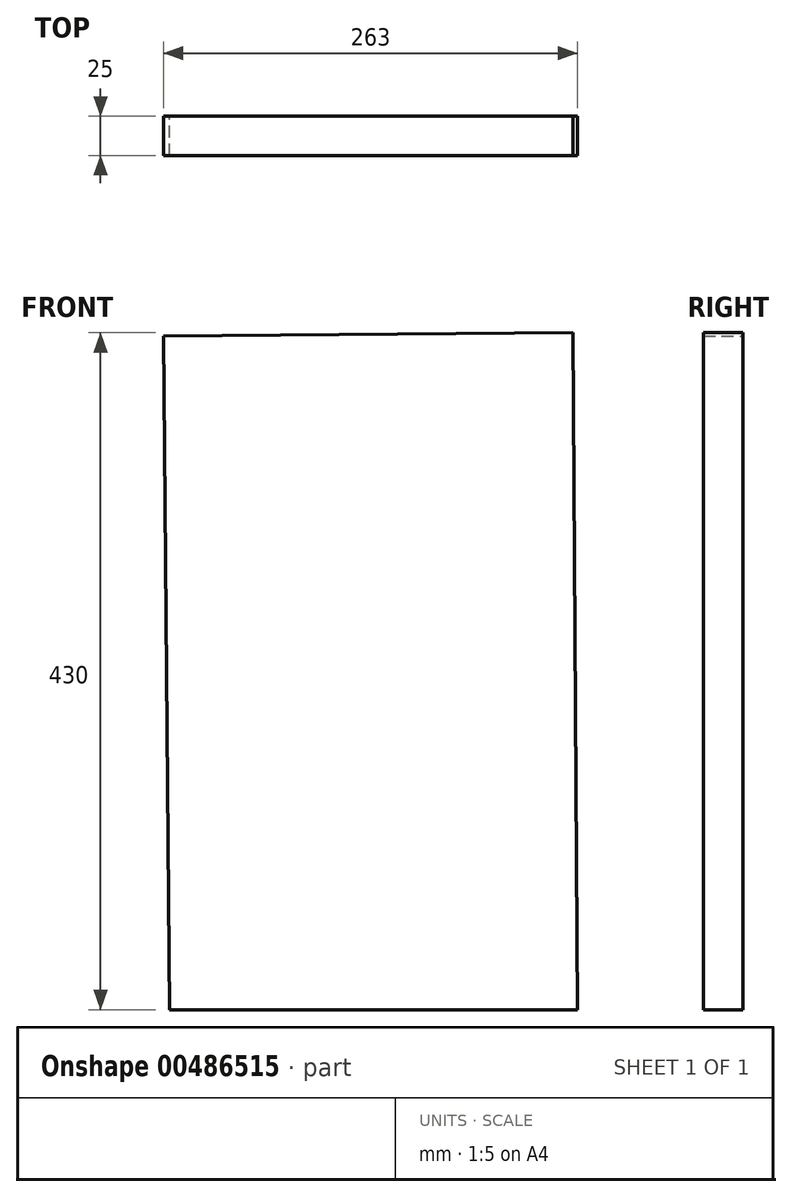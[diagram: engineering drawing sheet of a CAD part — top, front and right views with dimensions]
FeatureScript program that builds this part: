
annotation { "Feature Type Name" : "Feature", "Feature Type Description" : "" }
export const myFeature = defineFeature(function(context is Context, id is Id, definition is map)
    precondition{}
    {
        {
            var Q0;
            Q0=qCreatedBy(makeId("Front.planeOp"),FACE);
            var sketch = newSketch(context, id + "F0", { "sketchPlane" : qUnion([Q0])});
            skArc(sketch, "E0", {"start": v(777, 1224.97) * mm, "mid": v(1501.6, 922.35) * mm, "end": v(1800, 196) * mm});
            skLineSegment(sketch, "E1", {"start": v(1800, 196) * mm, "end": v(1800, 0) * mm});
            skLineSegment(sketch, "E2", {"start": v(1800, 0) * mm, "end": v(0, 0) * mm});
            skLineSegment(sketch, "E3", {"start": v(0, 0) * mm, "end": v(0, 611.22) * mm});
            skCircle(sketch, "E4", {"center": v(195, 100) * mm, "radius": 30 * mm});
            skLineSegment(sketch, "E5", {"start": v(911, 0) * mm, "end": v(908, 430) * mm});
            skLineSegment(sketch, "E6", {"start": v(648, 427.98) * mm, "end": v(908, 430) * mm});
            skLineSegment(sketch, "E7", {"start": v(-413, 1214) * mm, "end": v(-413, 956) * mm});
            skLineSegment(sketch, "E8", {"start": v(-413, 956) * mm, "end": v(0, 611.22) * mm});
            skLineSegment(sketch, "E9", {"start": v(-413, 1214) * mm, "end": v(777, 1224.97) * mm});
            skLineSegment(sketch, "E10", {"start": v(777, 1224.97) * mm, "end": v(777, 428.98) * mm});
            skLineSegment(sketch, "E11", {"start": v(648, 427.98) * mm, "end": v(652, 0) * mm});
            skSolve(sketch);
        }
        {
            var Q0;
            {var subQ1=sQuery(id+"F0.wireOp",EDGE,"E5");Q0=makeQuery(id+"F0.imprint","IMPRINT",FACE,{"disambiguationData":[TD([[makeQuery(id+"F0.imprint","IMPRINT",EDGE,{"derivedFrom":subQ1}),1.0]])]});}
            extrude(context, id + "F1", {"entities" : qUnion([Q0]), "depth" : 25 * mm, "offsetDistance" : 25 * mm});
        }
    });
